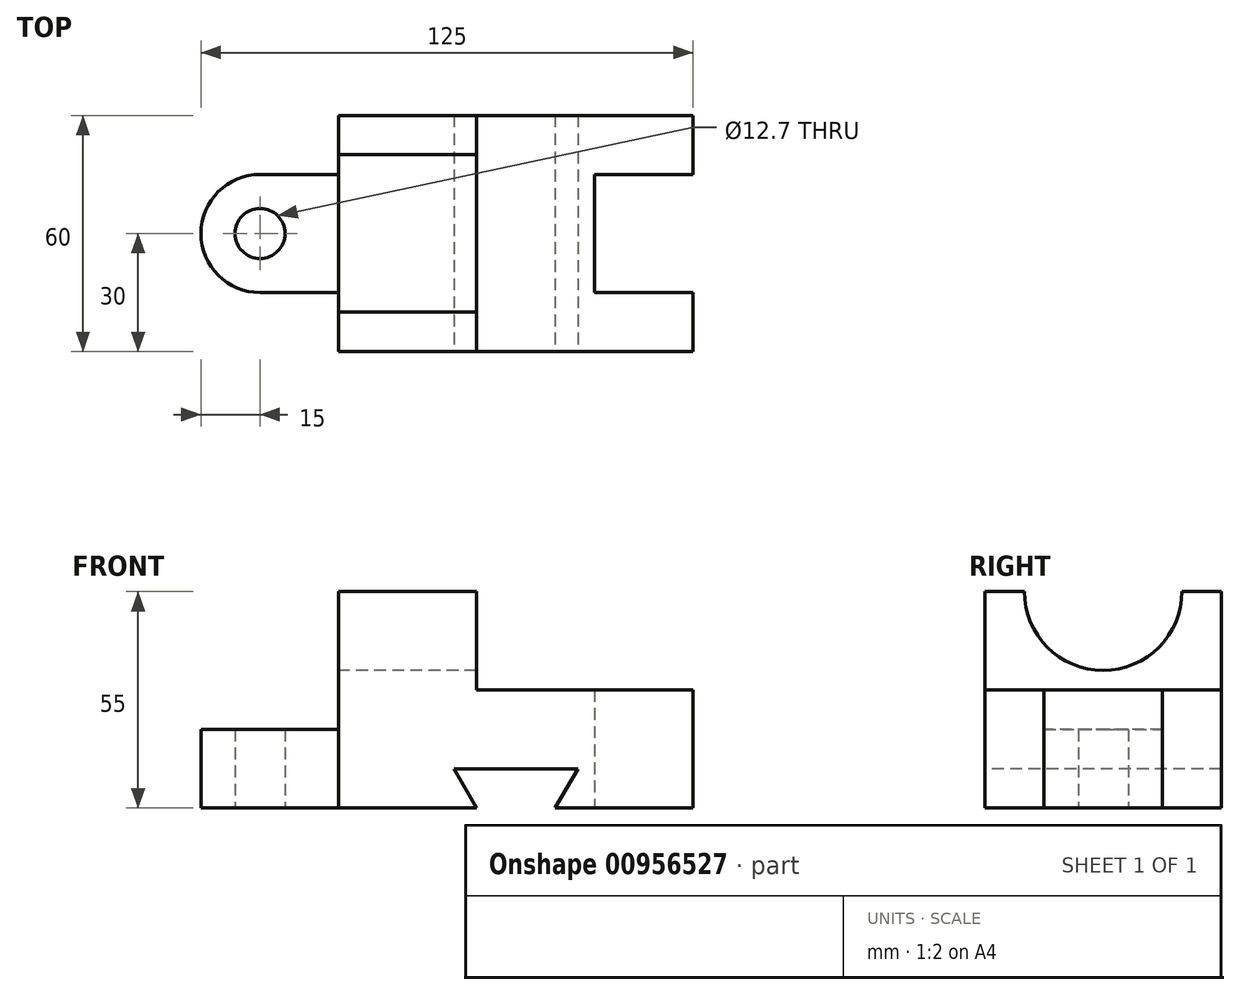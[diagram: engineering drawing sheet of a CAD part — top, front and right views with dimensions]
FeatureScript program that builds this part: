
annotation { "Feature Type Name" : "Feature", "Feature Type Description" : "" }
export const myFeature = defineFeature(function(context is Context, id is Id, definition is map)
    precondition{}
    {
        {
            var Q0;
            Q0=qCreatedBy(makeId("Top.planeOp"),FACE);
            var sketch = newSketch(context, id + "F0", { "sketchPlane" : qUnion([Q0])});
            skArc(sketch, "E0", {"start": v(0, 15) * mm, "mid": v(-15, 0) * mm, "end": v(0, -15) * mm});
            skCircle(sketch, "E1", {"center": v(0, 0) * mm, "radius": 6.35 * mm});
            skLineSegment(sketch, "E2", {"start": v(110, -15) * mm, "end": v(110, -30) * mm});
            skLineSegment(sketch, "E3", {"start": v(110, -30) * mm, "end": v(20, -30) * mm});
            skLineSegment(sketch, "E4", {"start": v(20, -30) * mm, "end": v(20, 30) * mm});
            skLineSegment(sketch, "E5", {"start": v(0, -15) * mm, "end": v(20, -15) * mm});
            skLineSegment(sketch, "E6", {"start": v(0, 15) * mm, "end": v(20, 15) * mm});
            skLineSegment(sketch, "E7", {"start": v(110, -15) * mm, "end": v(85, -15) * mm});
            skLineSegment(sketch, "E8", {"start": v(85, -15) * mm, "end": v(85, 15) * mm});
            skLineSegment(sketch, "E9", {"start": v(20, 30) * mm, "end": v(110, 30) * mm});
            skLineSegment(sketch, "E10", {"start": v(110, 30) * mm, "end": v(110, 15) * mm});
            skLineSegment(sketch, "E11", {"start": v(110, 15) * mm, "end": v(85, 15) * mm});
            skLineSegment(sketch, "E12", {"start": v(-56.23, 0) * mm, "end": v(166.24, 0) * mm, "construction": true});
            skLineSegment(sketch, "E13", {"start": v(55, 30) * mm, "end": v(55, -30) * mm});
            skSolve(sketch);
        }
        {
            var Q0;
            Q0=makeQuery(id+"F0.imprint","IMPRINT",FACE,{"disambiguationData":[TD([[makeQuery(id+"F0.imprint","IMPRINT",EDGE,{"derivedFrom":sQuery(id+"F0.wireOp",EDGE,"E0")}),1.0]])]});
            extrude(context, id + "F1", {"entities" : qUnion([Q0]), "depth" : 20 * mm, "offsetDistance" : 25 * mm});
        }
        {
            var Q0;
            {var subQ7=sQuery(id+"F0.wireOp",EDGE,"E13");Q0=makeQuery(id+"F0.imprint","IMPRINT",FACE,{"disambiguationData":[TD([[makeQuery(id+"F0.imprint","IMPRINT",EDGE,{"derivedFrom":subQ7}),-1.0]])]});}
            extrude(context, id + "F2", {"entities" : qUnion([Q0]), "operationType" : NewBodyOperationType.ADD, "depth" : 55 * mm, "offsetDistance" : 25 * mm});
        }
        {
            var Q0;
            {var subQ1=sQuery(id+"F0.wireOp",EDGE,"E2");Q0=makeQuery(id+"F0.imprint","IMPRINT",FACE,{"disambiguationData":[TD([[makeQuery(id+"F0.imprint","IMPRINT",EDGE,{"derivedFrom":subQ1}),-1.0]])]});}
            extrude(context, id + "F3", {"entities" : qUnion([Q0]), "operationType" : NewBodyOperationType.ADD, "depth" : 30 * mm, "offsetDistance" : 25 * mm});
        }
        {
            var Q0;
            Q0=makeQuery(id+"F2.opExtrude","SWEPT_FACE",FACE,{"disambiguationData":[OSD([sQuery(id+"F0.wireOp",EDGE,"E4")])]});
            var sketch = newSketch(context, id + "F4", { "sketchPlane" : qUnion([Q0])});
            skLineSegment(sketch, "E14", {"start": v(0, 62.55) * mm, "end": v(0, -17.43) * mm, "construction": true});
            skArc(sketch, "E15", {"start": v(-20, 55) * mm, "mid": v(0, 35) * mm, "end": v(20, 55) * mm});
            skLineSegment(sketch, "E16.0", {"start": v(20, 55) * mm, "end": v(-20, 55) * mm});
            skPoint(sketch, "E17.orphan", {"position": v(30, 55) * mm});
            skPoint(sketch, "E18.orphan", {"position": v(-30, 55) * mm});
            skSolve(sketch);
        }
        {
            var Q0;
            Q0=makeQuery(id+"F4.imprint","IMPRINT",FACE,{"disambiguationData":[TD([[makeQuery(id+"F4.imprint","IMPRINT",EDGE,{"derivedFrom":sQuery(id+"F4.wireOp",EDGE,"E15")}),1.0]])]});
            extrude(context, id + "F5", {"entities" : qUnion([Q0]), "operationType" : NewBodyOperationType.REMOVE, "endBound" : BoundingType.THROUGH_ALL, "oppositeDirection" : true, "depth" : 25 * mm, "offsetDistance" : 25 * mm});
        }
        {
            var Q0;
            {var subQ0=sQuery(id+"F0.wireOp",EDGE,"E3");Q0=makeQuery(id+"F3.boolean.opBoolean","MERGE",FACE,{"derivedFrom":[makeQuery(id+"F2.opExtrude","SWEPT_FACE",FACE,{"disambiguationData":[OSD([subQ0])]}),makeQuery(id+"F3.opExtrude","SWEPT_FACE",FACE,{"disambiguationData":[OSD([subQ0])]})]});}
            var sketch = newSketch(context, id + "F6", { "sketchPlane" : qUnion([Q0])});
            skLineSegment(sketch, "E19", {"start": v(75, -28.94) * mm, "end": v(75, 57.86) * mm, "construction": true});
            skLineSegment(sketch, "E20", {"start": v(75, 0) * mm, "end": v(80.77, 10) * mm});
            skLineSegment(sketch, "E21", {"start": v(80.77, 10) * mm, "end": v(49.23, 10) * mm});
            skLineSegment(sketch, "E22", {"start": v(49.23, 10) * mm, "end": v(55, 0) * mm});
            skLineSegment(sketch, "E23", {"start": v(55, 0) * mm, "end": v(75, 0) * mm});
            skSolve(sketch);
        }
        {
            var Q0;
            Q0=makeQuery(id+"F6.imprint","IMPRINT",FACE,{"disambiguationData":[TD([[makeQuery(id+"F6.imprint","IMPRINT",EDGE,{"derivedFrom":sQuery(id+"F6.wireOp",EDGE,"E20")}),1.0]])]});
            extrude(context, id + "F7", {"entities" : qUnion([Q0]), "operationType" : NewBodyOperationType.REMOVE, "endBound" : BoundingType.THROUGH_ALL, "oppositeDirection" : true, "depth" : 25 * mm, "offsetDistance" : 25 * mm});
        }
    });
